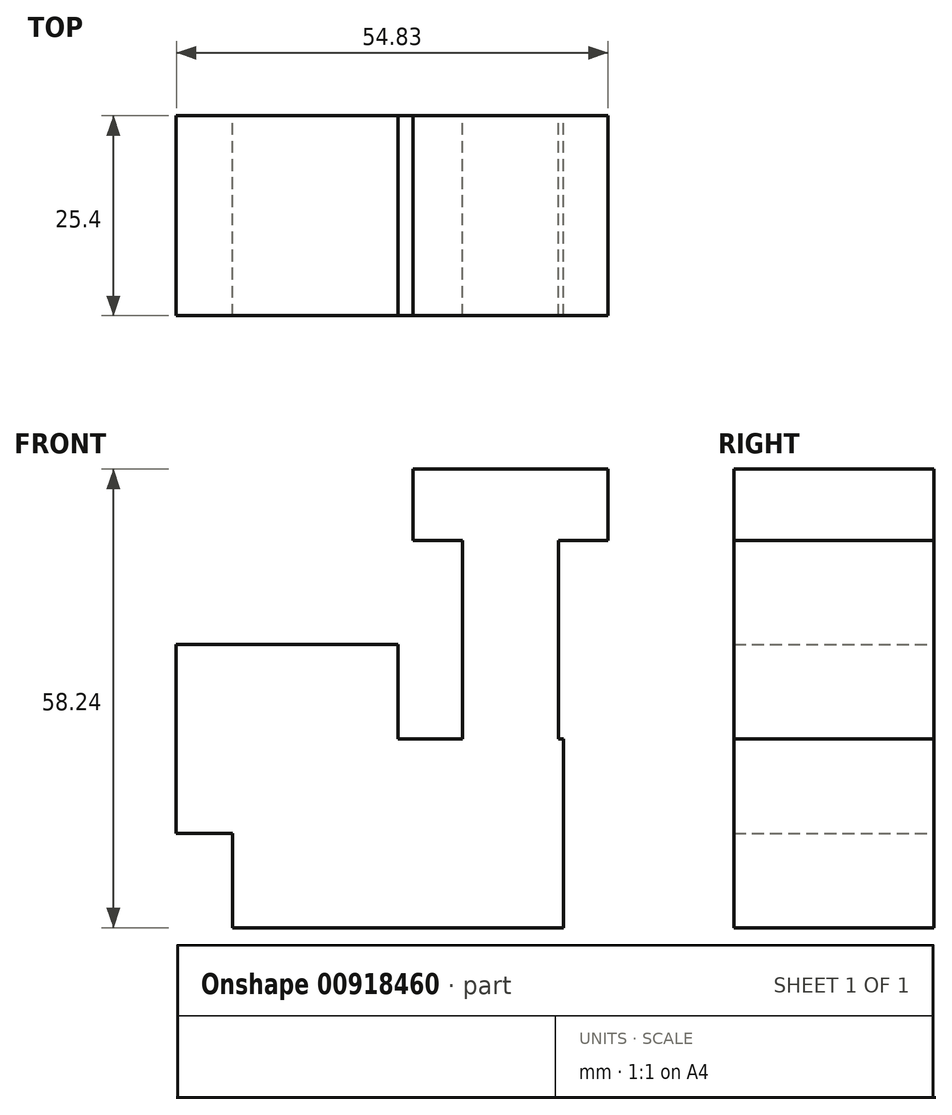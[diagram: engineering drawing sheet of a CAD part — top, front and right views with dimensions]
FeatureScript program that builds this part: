
annotation { "Feature Type Name" : "Feature", "Feature Type Description" : "" }
export const myFeature = defineFeature(function(context is Context, id is Id, definition is map)
    precondition{}
    {
        {
            var Q0;
            Q0=qCreatedBy(makeId("Front.planeOp"),FACE);
            var sketch = newSketch(context, id + "F0", { "sketchPlane" : qUnion([Q0])});
            skLineSegment(sketch, "E0.bottom", {"start": v(21.02, 0) * mm, "end": v(21.25, 0) * mm});
            skLineSegment(sketch, "E0.top", {"start": v(21.02, 0) * mm, "end": v(21.25, 0) * mm});
            skLineSegment(sketch, "E0.left", {"start": v(21.02, 0) * mm, "end": v(21.02, 0) * mm});
            skLineSegment(sketch, "E0.right", {"start": v(21.25, 0) * mm, "end": v(21.25, 0) * mm});
            skPoint(sketch, "E0.middle", {"position": v(21.14, 0) * mm});
            skLineSegment(sketch, "E1.bottom", {"start": v(0, -11.99) * mm, "end": v(-28.18, -11.99) * mm});
            skLineSegment(sketch, "E1.top", {"start": v(0, 11.99) * mm, "end": v(-28.18, 11.99) * mm});
            skLineSegment(sketch, "E1.left", {"start": v(0, -11.99) * mm, "end": v(0, 11.99) * mm});
            skLineSegment(sketch, "E1.right", {"start": v(-28.18, -11.99) * mm, "end": v(-28.18, 11.99) * mm});
            skPoint(sketch, "E1.middle", {"position": v(-14.1, 0) * mm});
            skLineSegment(sketch, "E2.bottom", {"start": v(21.02, 0) * mm, "end": v(-21.02, 0) * mm});
            skLineSegment(sketch, "E2.top", {"start": v(21.02, -23.97) * mm, "end": v(-21.02, -23.97) * mm});
            skLineSegment(sketch, "E2.left", {"start": v(21.02, 0) * mm, "end": v(21.02, -23.97) * mm});
            skLineSegment(sketch, "E2.right", {"start": v(-21.02, 0) * mm, "end": v(-21.02, -23.97) * mm});
            skPoint(sketch, "E2.middle", {"position": v(0, -11.99) * mm});
            skLineSegment(sketch, "E3.bottom", {"start": v(8.17, -9.73) * mm, "end": v(20.38, -9.73) * mm});
            skLineSegment(sketch, "E3.top", {"start": v(8.17, 29.73) * mm, "end": v(20.38, 29.73) * mm});
            skLineSegment(sketch, "E3.left", {"start": v(8.17, -9.73) * mm, "end": v(8.17, 29.73) * mm});
            skLineSegment(sketch, "E3.right", {"start": v(20.38, -9.73) * mm, "end": v(20.38, 29.73) * mm});
            skPoint(sketch, "E3.middle", {"position": v(14.28, 10) * mm});
            skLineSegment(sketch, "E4.bottom", {"start": v(26.65, 34.27) * mm, "end": v(1.9, 34.27) * mm});
            skLineSegment(sketch, "E4.top", {"start": v(26.65, 25.2) * mm, "end": v(1.9, 25.2) * mm});
            skLineSegment(sketch, "E4.left", {"start": v(26.65, 34.27) * mm, "end": v(26.65, 25.2) * mm});
            skLineSegment(sketch, "E4.right", {"start": v(1.9, 34.27) * mm, "end": v(1.9, 25.2) * mm});
            skPoint(sketch, "E4.middle", {"position": v(14.28, 29.73) * mm});
            skSolve(sketch);
        }
        {
            var Q0;
            Q0 = qSketchRegion(id + "F0", true);
            extrude(context, id + "F1", {"entities" : qUnion([Q0]), "depth" : 25.4 * mm, "offsetDistance" : 25.4 * mm});
        }
    });
